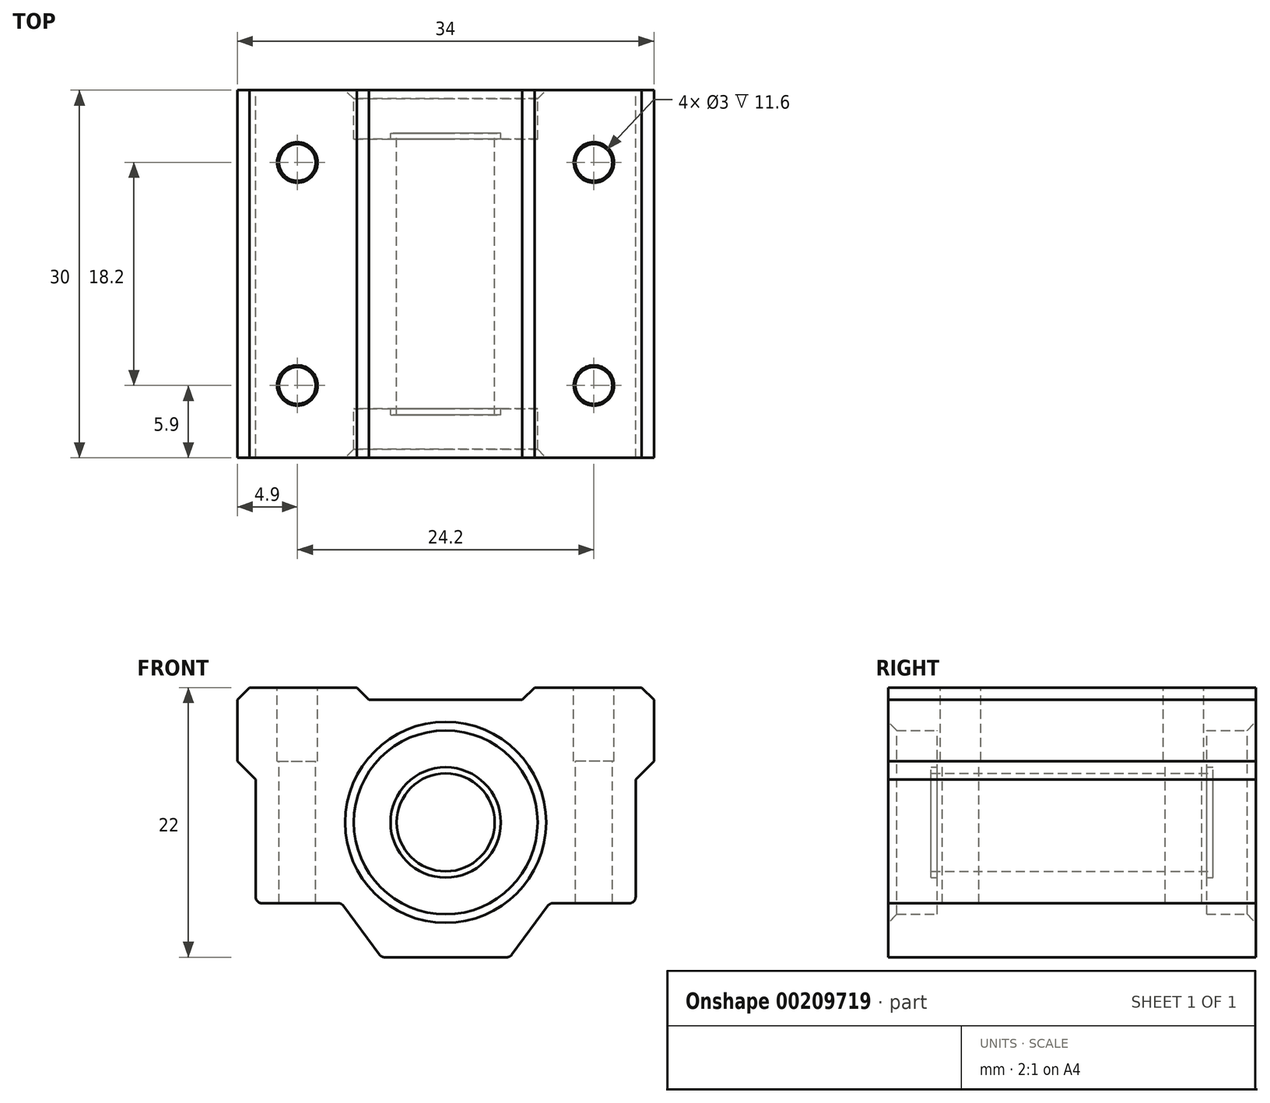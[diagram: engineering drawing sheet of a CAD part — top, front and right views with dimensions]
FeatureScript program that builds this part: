
annotation { "Feature Type Name" : "Feature", "Feature Type Description" : "" }
export const myFeature = defineFeature(function(context is Context, id is Id, definition is map)
    precondition{}
    {
        {
            var Q0;
            Q0=qCreatedBy(makeId("Front.planeOp"),FACE);
            var sketch = newSketch(context, id + "F0", { "sketchPlane" : qUnion([Q0])});
            skCircle(sketch, "E0", {"center": v(0, 0) * mm, "radius": 4 * mm});
            skCircle(sketch, "E1", {"center": v(0, 0) * mm, "radius": 7.5 * mm});
            skLineSegment(sketch, "E2", {"start": v(0, 0) * mm, "end": v(0, 22.9) * mm, "construction": true});
            skLineSegment(sketch, "E3", {"start": v(0, 7.5) * mm, "end": v(0, 10) * mm});
            skLineSegment(sketch, "E4", {"start": v(0, 10) * mm, "end": v(7.25, 10) * mm});
            skLineSegment(sketch, "E5", {"start": v(7.25, 10) * mm, "end": v(7.25, 11) * mm});
            skLineSegment(sketch, "E6", {"start": v(7.25, 11) * mm, "end": v(17, 11) * mm});
            skLineSegment(sketch, "E7", {"start": v(17, 11) * mm, "end": v(17, 3.5) * mm});
            skLineSegment(sketch, "E8", {"start": v(17, 3.5) * mm, "end": v(15.5, 3.5) * mm});
            skLineSegment(sketch, "E9", {"start": v(15.5, 3.5) * mm, "end": v(15.5, -6.6) * mm});
            skLineSegment(sketch, "E10", {"start": v(15.5, -6.6) * mm, "end": v(8.5, -6.6) * mm});
            skLineSegment(sketch, "E11", {"start": v(8.5, -6.6) * mm, "end": v(5.25, -11) * mm});
            skLineSegment(sketch, "E12", {"start": v(5.25, -11) * mm, "end": v(0, -11) * mm});
            skLineSegment(sketch, "E13", {"start": v(0, -11) * mm, "end": v(0, -7.5) * mm});
            skCircle(sketch, "E14", {"center": v(0, 0) * mm, "radius": 4.5 * mm});
            skSolve(sketch);
        }
        {
            var Q0;
            {var subQ0=sQuery(id+"F0.wireOp",EDGE,"E3");Q0=makeQuery(id+"F0.imprint","IMPRINT",FACE,{"disambiguationData":[TD([[makeQuery(id+"F0.imprint","IMPRINT",EDGE,{"derivedFrom":subQ0}),-1.0]])]});}
            extrude(context, id + "F1", {"entities" : qUnion([Q0]), "endBound" : BoundingType.SYMMETRIC, "depth" : 30 * mm});
        }
        {
            var Q0;
            Q0=makeQuery(id+"F1.opExtrude","SWEPT_EDGE",EDGE,{"disambiguationData":[OSD([sQuery(id+"F0.wireOp",EDGE,"E4"),sQuery(id+"F0.wireOp",EDGE,"E5")])]});
            var Q1;
            Q1=makeQuery(id+"F1.opExtrude","SWEPT_EDGE",EDGE,{"disambiguationData":[OSD([sQuery(id+"F0.wireOp",EDGE,"E6"),sQuery(id+"F0.wireOp",EDGE,"E7")])]});
            chamfer(context, id + "F2", {"entities" : qUnion([Q0, Q1]), "width" : 1 * mm, "tangentPropagation" : true});
        }
        {
            var Q0;
            Q0=makeQuery(id+"F1.opExtrude","SWEPT_EDGE",EDGE,{"disambiguationData":[OSD([sQuery(id+"F0.wireOp",EDGE,"E7"),sQuery(id+"F0.wireOp",EDGE,"E8")])]});
            chamfer(context, id + "F3", {"entities" : qUnion([Q0]), "width" : 1.5 * mm, "tangentPropagation" : true});
        }
        {
            var Q0;
            Q0=makeQuery(id+"F1.opExtrude","SWEPT_EDGE",EDGE,{"disambiguationData":[OSD([sQuery(id+"F0.wireOp",EDGE,"E9"),sQuery(id+"F0.wireOp",EDGE,"E10")])]});
            var Q1;
            Q1=makeQuery(id+"F1.opExtrude","SWEPT_EDGE",EDGE,{"disambiguationData":[OSD([sQuery(id+"F0.wireOp",EDGE,"E10"),sQuery(id+"F0.wireOp",EDGE,"E11")])]});
            var Q2;
            Q2=makeQuery(id+"F1.opExtrude","SWEPT_EDGE",EDGE,{"disambiguationData":[OSD([sQuery(id+"F0.wireOp",EDGE,"E11"),sQuery(id+"F0.wireOp",EDGE,"E12")])]});
            fillet(context, id + "F4", {"entities" : qUnion([Q0, Q1, Q2]), "radius" : .5 * mm, "tangentPropagation" : true, "allowEdgeOverflow" : false});
        }
        {
            var Q0;
            Q0=makeQuery(id+"F1.opExtrude","SWEPT_FACE",FACE,{"disambiguationData":[OSD([sQuery(id+"F0.wireOp",EDGE,"E6")])]});
            var sketch = newSketch(context, id + "F5", { "sketchPlane" : qUnion([Q0])});
            skLineSegment(sketch, "E15.bottom", {"start": v(-12.1, 9.1) * mm, "end": v(12.1, 9.1) * mm});
            skLineSegment(sketch, "E15.top", {"start": v(-12.1, -9.1) * mm, "end": v(12.1, -9.1) * mm});
            skLineSegment(sketch, "E15.left", {"start": v(-12.1, 9.1) * mm, "end": v(-12.1, -9.1) * mm});
            skLineSegment(sketch, "E15.right", {"start": v(12.1, 9.1) * mm, "end": v(12.1, -9.1) * mm});
            skLineSegment(sketch, "E16", {"start": v(-12.1, 9.1) * mm, "end": v(12.1, -9.1) * mm});
            skSolve(sketch);
        }
        {
            var Q0;
            Q0=sQuery(id+"F5.wireOp",VERTEX,"E15.right.start");
            var Q1;
            Q1=sQuery(id+"F5.wireOp",VERTEX,"E16.end");
            var Q2;
            Q2=makeQuery(id+"F1.opExtrude","SWEPT_BODY",BODY,{"disambiguationData":[OSD([sQuery(id+"F0.wireOp",EDGE,"E1"),sQuery(id+"F0.wireOp",EDGE,"E3"),sQuery(id+"F0.wireOp",EDGE,"E4"),sQuery(id+"F0.wireOp",EDGE,"E5"),sQuery(id+"F0.wireOp",EDGE,"E6"),sQuery(id+"F0.wireOp",EDGE,"E7"),sQuery(id+"F0.wireOp",EDGE,"E8"),sQuery(id+"F0.wireOp",EDGE,"E9"),sQuery(id+"F0.wireOp",EDGE,"E10"),sQuery(id+"F0.wireOp",EDGE,"E11"),sQuery(id+"F0.wireOp",EDGE,"E12"),sQuery(id+"F0.wireOp",EDGE,"E13")])]});
            hole(context, id + "F6", {"style" : HoleStyle.C_BORE, "endStyle" : HoleEndStyle.THROUGH, "holeDiameter" : 3 * mm, "cBoreDiameter" : 3.3 * mm, "cBoreDepth" : 6 * mm, "locations" : qUnion([Q0, Q1]), "scope" : qUnion([Q2]), "isTappedThrough" : true});
        }
        {
            var Q0;
            Q0=makeQuery(id+"F6.hole-1.boolean.opBoolean","COPY",EDGE,{"derivedFrom":makeQuery(id+"F6.hole-1.opRevolve","SWEPT_EDGE",EDGE,{"disambiguationData":[OSD([sQuery(id+"F6.hole-1.sketch.wireOp",EDGE,"cbore_start_line_2"),sQuery(id+"F6.hole-1.sketch.wireOp",EDGE,"cbore_start_line_3")])]})});
            var Q1;
            Q1=makeQuery(id+"F6.hole-0.boolean.opBoolean","COPY",EDGE,{"derivedFrom":makeQuery(id+"F6.hole-0.opRevolve","SWEPT_EDGE",EDGE,{"disambiguationData":[OSD([sQuery(id+"F6.hole-0.sketch.wireOp",EDGE,"cbore_start_line_2"),sQuery(id+"F6.hole-0.sketch.wireOp",EDGE,"cbore_start_line_3")])]})});
            var Q2;
            Q2=makeQuery(id+"F1.opExtrude","CAP_EDGE",EDGE,{"disambiguationData":[OSD([sQuery(id+"F0.wireOp",EDGE,"E1")])],"isStart":false});
            var Q3;
            Q3=makeQuery(id+"F1.opExtrude","CAP_EDGE",EDGE,{"disambiguationData":[OSD([sQuery(id+"F0.wireOp",EDGE,"E1")])],"isStart":true});
            chamfer(context, id + "F7", {"entities" : qUnion([Q0, Q1, Q2, Q3]), "width" : .7 * mm, "tangentPropagation" : true});
        }
        {
            var Q0;
            Q0=makeQuery(id+"F0.imprint","IMPRINT",FACE,{"disambiguationData":[TD([[makeQuery(id+"F0.imprint","IMPRINT",EDGE,{"derivedFrom":sQuery(id+"F0.wireOp",EDGE,"E14")}),-1.0]])]});
            extrude(context, id + "F8", {"entities" : qUnion([Q0]), "endBound" : BoundingType.SYMMETRIC, "depth" : 22 * mm});
        }
        {
            var Q0;
            Q0=makeQuery(id+"F0.imprint","IMPRINT",FACE,{"disambiguationData":[TD([[makeQuery(id+"F0.imprint","IMPRINT",EDGE,{"derivedFrom":sQuery(id+"F0.wireOp",EDGE,"E0")}),-1.0]])]});
            extrude(context, id + "F9", {"entities" : qUnion([Q0]), "operationType" : NewBodyOperationType.ADD, "endBound" : BoundingType.SYMMETRIC, "depth" : 23 * mm});
        }
        {
            var Q0;
            Q0=makeQuery(id+"F1.opExtrude","SWEPT_BODY",BODY,{"disambiguationData":[OSD([sQuery(id+"F0.wireOp",EDGE,"E1"),sQuery(id+"F0.wireOp",EDGE,"E3"),sQuery(id+"F0.wireOp",EDGE,"E4"),sQuery(id+"F0.wireOp",EDGE,"E5"),sQuery(id+"F0.wireOp",EDGE,"E6"),sQuery(id+"F0.wireOp",EDGE,"E7"),sQuery(id+"F0.wireOp",EDGE,"E8"),sQuery(id+"F0.wireOp",EDGE,"E9"),sQuery(id+"F0.wireOp",EDGE,"E10"),sQuery(id+"F0.wireOp",EDGE,"E11"),sQuery(id+"F0.wireOp",EDGE,"E12"),sQuery(id+"F0.wireOp",EDGE,"E13")])]});
            var Q1;
            Q1=qCreatedBy(makeId("Right.planeOp"),FACE);
            mirror(context, id + "F10", {"operationType" : NewBodyOperationType.ADD, "entities" : qUnion([Q0]), "mirrorPlane" : qUnion([Q1])});
        }
    });
